FCSTD DOCUMENT  (FreeCAD 0.19RUnknown)
Label: egg
License: All rights reserved
LicenseURL: http://en.wikipedia.org/wiki/All_rights_reserved
objects: Sketcher::SketchObject×2
note: 2 computed .brp shape members not serialized (recipe doc carries the construction recipe); baked Part::Feature solids carry a one-line shape summary decoded from their .brp

FEATURE [Sketcher::SketchObject] Sketch
  FullyConstrained = true
  Placement = pos=(0,0,0) rot=(1,0,0;1.5708rad)
  sketch-geometry (34):
    g0: LineSegment StartX=0 StartY=0 StartZ=0 EndX=0 EndY=53 EndZ=0
    g1: LineSegment StartX=-20 StartY=20 StartZ=0 EndX=20 EndY=20 EndZ=0
    g2: ArcOfCircle CenterX=1e-16 CenterY=20 CenterZ=0 NormalX=0 NormalY=0 NormalZ=1 AngleXU=0 Radius=20 StartAngle=3.14159 EndAngle=6.28319
    g3: ArcOfCircle CenterX=17.225 CenterY=20 CenterZ=0 NormalX=0 NormalY=0 NormalZ=1 AngleXU=0 Radius=37.225 StartAngle=2.05186 EndAngle=3.14159
    g4: ArcOfCircle CenterX=-17.225 CenterY=20 CenterZ=0 NormalX=0 NormalY=0 NormalZ=1 AngleXU=0 Radius=37.225 StartAngle=1e-16 EndAngle=1.08973
    g5: GeomPoint X=0 Y=-3 Z=0
    g6: LineSegment StartX=0 StartY=-3 StartZ=0 EndX=-35 EndY=-3 EndZ=0
    g7: GeomPoint X=20 Y=20 Z=0
    g8: ArcOfCircle CenterX=1e-16 CenterY=20 CenterZ=0 NormalX=0 NormalY=0 NormalZ=1 AngleXU=0 Radius=20 StartAngle=3.14159 EndAngle=6.28319
    g9: GeomPoint X=23.5 Y=20 Z=0
    g10: GeomPoint X=35 Y=-3 Z=0
    g11: LineSegment StartX=0 StartY=-3 StartZ=0 EndX=35 EndY=-3 EndZ=0
    g12: LineSegment StartX=-20 StartY=20 StartZ=0 EndX=-23.5 EndY=20 EndZ=0
    g13: LineSegment StartX=-23.5 StartY=20 StartZ=0 EndX=-23.5 EndY=26 EndZ=0
    g14: LineSegment StartX=-23.5 StartY=26 StartZ=0 EndX=-21.5 EndY=26 EndZ=0
    g15: LineSegment StartX=-20 StartY=21 StartZ=0 EndX=-20 EndY=20 EndZ=0
    g16: GeomPoint X=20 Y=21 Z=0
    g17: ArcOfCircle CenterX=-50.2935 CenterY=20 CenterZ=0 NormalX=0 NormalY=0 NormalZ=1 AngleXU=0 Radius=26.7935 StartAngle=5.31986 EndAngle=6.28319
    g18: GeomPoint X=50.2935 Y=20 Z=0
    g19: ArcOfCircle CenterX=50.2935 CenterY=20 CenterZ=0 NormalX=0 NormalY=0 NormalZ=1 AngleXU=0 Radius=26.7935 StartAngle=3.14159 EndAngle=4.10492
    g20: LineSegment StartX=-35 StartY=-3 StartZ=0 EndX=-35 EndY=-2 EndZ=0
    g21: LineSegment StartX=35 StartY=-3 StartZ=0 EndX=35 EndY=-2 EndZ=0
    g22: ArcOfCircle CenterX=-29.0833 CenterY=21 CenterZ=0 NormalX=0 NormalY=0 NormalZ=1 AngleXU=0 Radius=9.08333 StartAngle=3e-16 EndAngle=0.582914
    g23: ArcOfCircle CenterX=-22.5 CenterY=25 CenterZ=0 NormalX=0 NormalY=0 NormalZ=1 AngleXU=0 Radius=1 StartAngle=1.5708 EndAngle=3.14159
    g24: LineSegment StartX=-22.5 StartY=26 StartZ=0 EndX=-21.5 EndY=26 EndZ=0
    g25: LineSegment StartX=-23.5 StartY=25 StartZ=0 EndX=-23.5 EndY=20 EndZ=0
    g26: LineSegment StartX=20 StartY=20 StartZ=0 EndX=20 EndY=21 EndZ=0
    g27: GeomPoint X=21.5 Y=26 Z=0
    g28: GeomPoint X=22.5 Y=26 Z=0
    g29: GeomPoint X=22.5 Y=25 Z=0
    g30: LineSegment StartX=23.5 StartY=20 StartZ=0 EndX=23.5 EndY=25 EndZ=0
    g31: ArcOfCircle CenterX=22.5 CenterY=25 CenterZ=0 NormalX=0 NormalY=0 NormalZ=1 AngleXU=0 Radius=1 StartAngle=-1.8e-15 EndAngle=1.5708
    g32: LineSegment StartX=22.5 StartY=26 StartZ=0 EndX=21.5 EndY=26 EndZ=0
    g33: ArcOfCircle CenterX=29.0833 CenterY=21 CenterZ=0 NormalX=0 NormalY=0 NormalZ=1 AngleXU=0 Radius=9.08333 StartAngle=2.55868 EndAngle=3.14159
  constraints (77):
    c: Coincident(g0,g-1)
    c: Symmetric(g1,g1,g0)
    c: DistanceX(g1,g1) = 40
    c: DistanceY(g0,g0) = 53
    c: Coincident(g2,g1)
    c: Coincident(g2,g1)
    c: PointOnObject(g0,g2)
    c: PointOnObject(g2,g1)
    c: PointOnObject(g3,g1)
    c: Coincident(g3,g1)
    c: Coincident(g3,g0)
    c: PointOnObject(g4,g1)
    c: Coincident(g4,g1)
    c: Coincident(g4,g0)
    c: PointOnObject(g5,g-2)
    c: DistanceY(g5,g-1) = 3
    c: Coincident(g6,g5)
    c: Horizontal(g6)
    c: DistanceX(g12,g1) = 3.5
    c: Symmetric(g8,g7,g0)
    c: Coincident(g8,g2)
    c: Coincident(g8,g7)
    c: Symmetric(g9,g12,g0)
    c: Symmetric(g10,g6,g-2)
    c: Coincident(g11,g6)
    c: Coincident(g11,g10)
    c: Coincident(g8,g1)
    c: Coincident(g12,g8)
    c: Horizontal(g12)
    c: Vertical(g13)
    c: DistanceY(g13,g13) = 6
    c: Coincident(g14,g13)
    c: Horizontal(g14)
    c: Coincident(g15,g8)
    c: Vertical(g15)
    c: Symmetric(g16,g15,g0)
    c: DistanceY(g6,g17) = 1
    c: Coincident(g17,g13)
    c: Symmetric(g18,g17,g0)
    c: Coincident(g19,g18)
    c: Coincident(g19,g9) = 1.5708
    c: Coincident(g13,g12)
    c: DistanceX(g6,g6) = 35
    c: Coincident(g20,g6)
    c: Coincident(g20,g17)
    c: Vertical(g20)
    c: Coincident(g21,g11)
    c: Vertical(g21)
    c: Coincident(g19,g21)
    c: DistanceX(g14,g14) = 2
    c: Coincident(g22,g14)
    c: DistanceY(g15,g15) = 1
    c: Tangent(g22,g15) = 1.5708
    c: Tangent(g23,g13) = 1.5708
    c: DistanceX(g23,g22) = 1
    c: Coincident(g24,g22)
    c: Coincident(g25,g23)
    c: Tangent(g23,g24) = 1.5708
    c: PointOnObject(g23,g14)
    c: Tangent(g25,g17) = 1.5708
    c: Coincident(g26,g8)
    c: Coincident(g26,g16)
    c: Vertical(g26)
    c: Symmetric(g22,g27,g0)
    c: Symmetric(g28,g23,g0)
    c: Symmetric(g29,g23,g0)
    c: Coincident(g30,g19)
    c: Symmetric(g30,g23,g0)
    c: Coincident(g31,g29)
    c: Coincident(g31,g30)
    c: Coincident(g31,g28)
    c: Coincident(g32,g31)
    c: Coincident(g32,g27)
    c: Horizontal(g32)
    c: Coincident(g33,g32)
    c: Coincident(g33,g26)
    c: Symmetric(g22,g33,g0)
FEATURE [Sketcher::SketchObject] Sketch001
  FullyConstrained = true
  Placement = pos=(0,0,0) rot=(1,0,0;1.5708rad)
  sketch-geometry (21):
    g0: LineSegment StartX=0 StartY=0 StartZ=0 EndX=0 EndY=53 EndZ=0
    g1: LineSegment StartX=-20 StartY=20 StartZ=0 EndX=20 EndY=20 EndZ=0
    g2: ArcOfCircle CenterX=-1.5e-15 CenterY=20 CenterZ=0 NormalX=0 NormalY=0 NormalZ=1 AngleXU=0 Radius=20 StartAngle=3.14159 EndAngle=6.28319
    g3: ArcOfCircle CenterX=17.225 CenterY=20 CenterZ=0 NormalX=0 NormalY=0 NormalZ=1 AngleXU=0 Radius=37.225 StartAngle=2.05186 EndAngle=3.14159
    g4: ArcOfCircle CenterX=-17.225 CenterY=20 CenterZ=0 NormalX=0 NormalY=0 NormalZ=1 AngleXU=0 Radius=37.225 StartAngle=0 EndAngle=1.08973
    g5: GeomPoint X=0 Y=-3 Z=0
    g6: LineSegment StartX=0 StartY=-3 StartZ=0 EndX=-35 EndY=-3 EndZ=0
    g7: GeomPoint X=20 Y=20 Z=0
    g8: LineSegment StartX=-20 StartY=20 StartZ=0 EndX=-23.5 EndY=20 EndZ=0
    g9: LineSegment StartX=-23.5 StartY=20 StartZ=0 EndX=-23.5 EndY=26 EndZ=0
    g10: LineSegment StartX=-23.5 StartY=26 StartZ=0 EndX=-21.5 EndY=26 EndZ=0
    g11: LineSegment StartX=-20 StartY=21 StartZ=0 EndX=-20 EndY=20 EndZ=0
    g12: GeomPoint X=20 Y=21 Z=0
    g13: ArcOfCircle CenterX=-50.2935 CenterY=20 CenterZ=0 NormalX=0 NormalY=0 NormalZ=1 AngleXU=0 Radius=26.7935 StartAngle=5.31986 EndAngle=6.28319
    g14: LineSegment StartX=-35 StartY=-3 StartZ=0 EndX=-35 EndY=-2 EndZ=0
    g15: ArcOfCircle CenterX=-29.0833 CenterY=21 CenterZ=0 NormalX=0 NormalY=0 NormalZ=1 AngleXU=0 Radius=9.08333 StartAngle=3e-16 EndAngle=0.582914
    g16: ArcOfCircle CenterX=-22.5 CenterY=25 CenterZ=0 NormalX=0 NormalY=0 NormalZ=1 AngleXU=0 Radius=1 StartAngle=1.5708 EndAngle=3.14159
    g17: LineSegment StartX=-22.5 StartY=26 StartZ=0 EndX=-21.5 EndY=26 EndZ=0
    g18: LineSegment StartX=-23.5 StartY=25 StartZ=0 EndX=-23.5 EndY=20 EndZ=0
    g19: ArcOfCircle CenterX=-1.5e-15 CenterY=20 CenterZ=0 NormalX=0 NormalY=0 NormalZ=1 AngleXU=0 Radius=20 StartAngle=3.14159 EndAngle=4.71239
    g20: LineSegment StartX=-5.1e-15 StartY=0 StartZ=0 EndX=0 EndY=-3 EndZ=0
  constraints (53):
    c: Coincident(g0,g-1)
    c: Symmetric(g1,g1,g0)
    c: DistanceX(g1,g1) = 40
    c: DistanceY(g0,g0) = 53
    c: Coincident(g2,g1)
    c: Coincident(g2,g1)
    c: PointOnObject(g0,g2)
    c: PointOnObject(g2,g1)
    c: PointOnObject(g3,g1)
    c: Coincident(g3,g1)
    c: Coincident(g3,g0)
    c: PointOnObject(g4,g1)
    c: Coincident(g4,g1)
    c: Coincident(g4,g0)
    c: PointOnObject(g5,g-2)
    c: DistanceY(g5,g-1) = 3
    c: Coincident(g6,g5)
    c: Horizontal(g6)
    c: DistanceX(g8,g1) = 3.5
    c: Symmetric(g1,g7,g0)
    c: Horizontal(g8)
    c: Vertical(g9)
    c: DistanceY(g9,g9) = 6
    c: Coincident(g10,g9)
    c: Horizontal(g10)
    c: Vertical(g11)
    c: Symmetric(g12,g11,g0)
    c: DistanceY(g6,g13) = 1
    c: Coincident(g13,g9)
    c: Coincident(g9,g8)
    c: DistanceX(g6,g6) = 35
    c: Coincident(g14,g6)
    c: Coincident(g14,g13)
    c: Vertical(g14)
    c: DistanceX(g10,g10) = 2
    c: Coincident(g15,g10)
    c: DistanceY(g11,g11) = 1
    c: Tangent(g15,g11) = 1.5708
    c: Tangent(g16,g9) = 1.5708
    c: DistanceX(g16,g15) = 1
    c: Coincident(g17,g15)
    c: Coincident(g18,g16)
    c: Tangent(g16,g17) = 1.5708
    c: PointOnObject(g16,g10)
    c: Tangent(g18,g13) = 1.5708
    c: Coincident(g19,g2)
    c: Coincident(g19,g11)
    c: Coincident(g19,g-1)
    c: Horizontal(g1)
    c: Coincident(g20,g19)
    c: Coincident(g20,g6)
    c: Coincident(g8,g11)
    c: PointOnObject(g11,g1)
